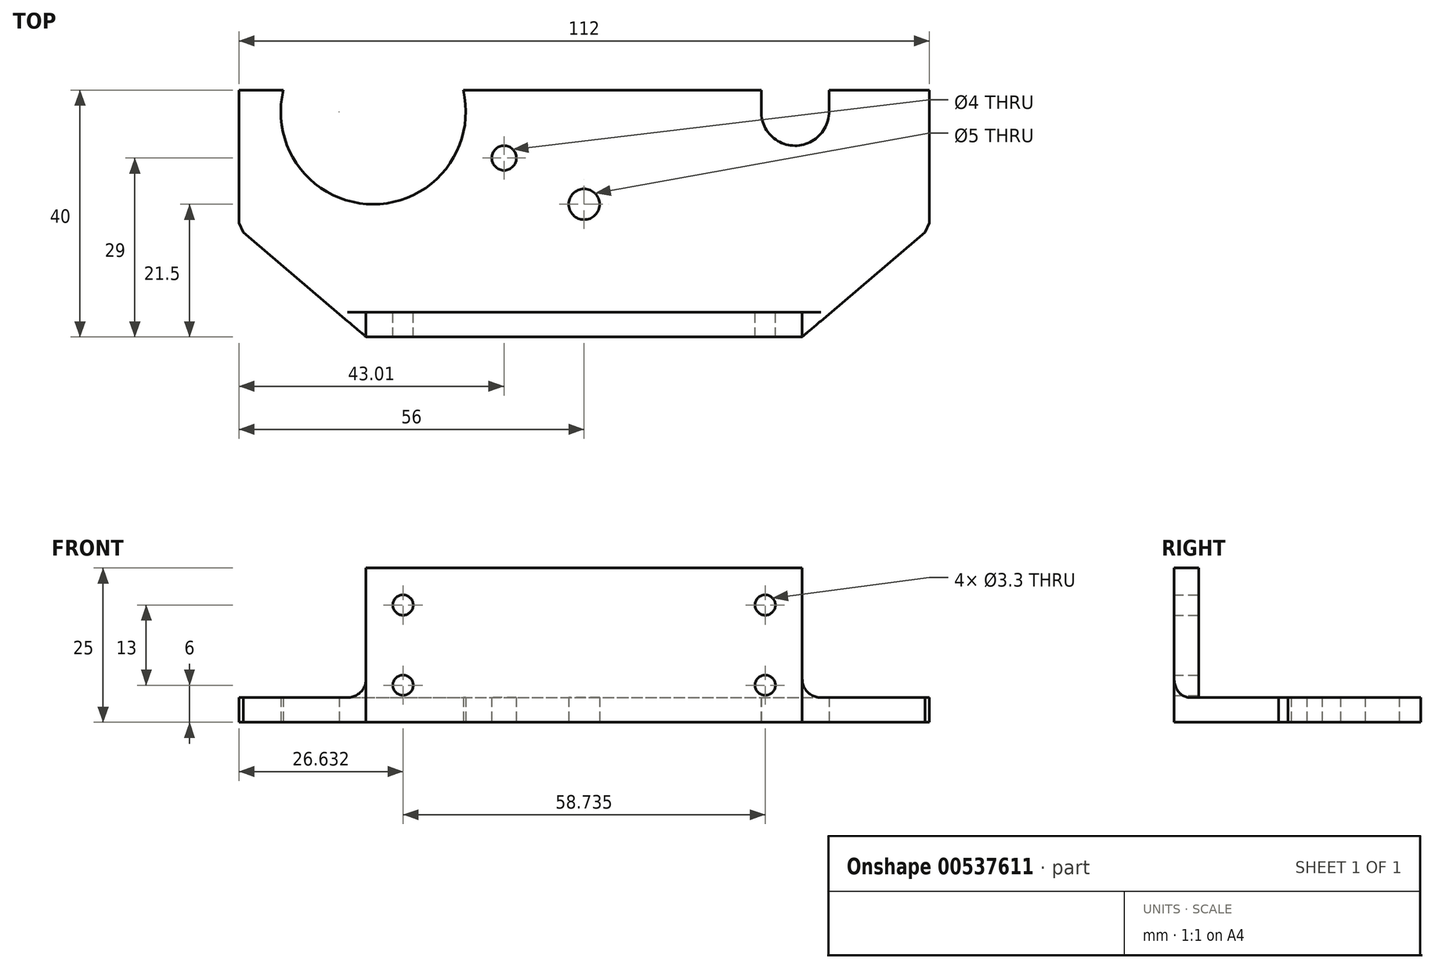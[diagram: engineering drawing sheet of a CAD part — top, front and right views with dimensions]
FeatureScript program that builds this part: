
annotation { "Feature Type Name" : "Feature", "Feature Type Description" : "" }
export const myFeature = defineFeature(function(context is Context, id is Id, definition is map)
    precondition{}
    {
        {
            var Q0;
            Q0=qCreatedBy(makeId("Top.planeOp"),FACE);
            var sketch = newSketch(context, id + "F0", { "sketchPlane" : qUnion([Q0])});
            skCircle(sketch, "E0", {"center": v(0, 0) * mm, "radius": 2.5 * mm});
            skCircle(sketch, "E1", {"center": v(0, 0) * mm, "radius": 18.5 * mm});
            skCircle(sketch, "E2", {"center": v(0, 0) * mm, "radius": 7.5 * mm});
            skCircle(sketch, "E3", {"center": v(-13, 7.5) * mm, "radius": 7.5 * mm});
            skCircle(sketch, "E4", {"center": v(-34.2, 15) * mm, "radius": 15 * mm});
            skCircle(sketch, "E5", {"center": v(-13, 7.5) * mm, "radius": 2 * mm});
            skCircle(sketch, "E6", {"center": v(-34.2, 15) * mm, "radius": 5.5 * mm});
            skLineSegment(sketch, "E7", {"start": v(0, 18.5) * mm, "end": v(-55, 18.5) * mm});
            skLineSegment(sketch, "E8", {"start": v(-55, 18.5) * mm, "end": v(-55, -3.5) * mm});
            skLineSegment(sketch, "E9", {"start": v(0, 18.5) * mm, "end": v(55, 18.5) * mm});
            skLineSegment(sketch, "E10", {"start": v(55, 18.5) * mm, "end": v(55, -3.5) * mm});
            skLineSegment(sketch, "E11", {"start": v(0, -20.5) * mm, "end": v(35, -20.5) * mm});
            skLineSegment(sketch, "E12", {"start": v(35, -20.5) * mm, "end": v(55, -3.5) * mm});
            skLineSegment(sketch, "E13", {"start": v(0, -20.5) * mm, "end": v(-35, -20.5) * mm});
            skLineSegment(sketch, "E14", {"start": v(-35, -20.5) * mm, "end": v(-55, -3.5) * mm});
            skLineSegment(sketch, "E15", {"start": v(-39.7, 14.97) * mm, "end": v(-39.7, 18.5) * mm});
            skLineSegment(sketch, "E16", {"start": v(-28.7, 15.1) * mm, "end": v(-28.76, 18.5) * mm});
            skCircle(sketch, "E17.MirrorC", {"center": v(34.2, 15) * mm, "radius": 5.5 * mm});
            skLineSegment(sketch, "E18.MirrorCS", {"start": v(28.7, 15.1) * mm, "end": v(28.76, 18.5) * mm});
            skLineSegment(sketch, "E19.MirrorCS", {"start": v(39.7, 14.97) * mm, "end": v(39.7, 18.5) * mm});
            skLineSegment(sketch, "E20.0", {"start": v(-56, 18.5) * mm, "end": v(-56, -3.96) * mm});
            skLineSegment(sketch, "E20.1", {"start": v(-35.37, -21.5) * mm, "end": v(-56, -3.96) * mm});
            skLineSegment(sketch, "E20.2", {"start": v(56, 18.5) * mm, "end": v(56, -3.96) * mm});
            skLineSegment(sketch, "E20.3", {"start": v(35.37, -21.5) * mm, "end": v(56, -3.96) * mm});
            skLineSegment(sketch, "E20.4", {"start": v(0, -21.5) * mm, "end": v(35.37, -21.5) * mm});
            skLineSegment(sketch, "E20.5", {"start": v(0, -21.5) * mm, "end": v(-35.37, -21.5) * mm});
            skLineSegment(sketch, "E21", {"start": v(56, 18.5) * mm, "end": v(55, 18.5) * mm});
            skLineSegment(sketch, "E22", {"start": v(-55, 18.5) * mm, "end": v(-56, 18.5) * mm});
            skSolve(sketch);
        }
        {
            var Q0;
            {var subQ12=sQuery(id+"F0.wireOp",EDGE,"E8");Q0=makeQuery(id+"F0.imprint","IMPRINT",FACE,{"disambiguationData":[TD([[makeQuery(id+"F0.imprint","IMPRINT",EDGE,{"derivedFrom":subQ12}),1.0]])]});}
            var Q1;
            {var subQ1=sQuery(id+"F0.wireOp",EDGE,"E2");Q1=makeQuery(id+"F0.imprint","IMPRINT",FACE,{"disambiguationData":[TD([[makeQuery(id+"F0.imprint","IMPRINT",EDGE,{"derivedFrom":subQ1}),-1.0]])]});}
            var Q2;
            Q2=makeQuery(id+"F0.imprint","IMPRINT",FACE,{"disambiguationData":[TD([[makeQuery(id+"F0.imprint","IMPRINT",EDGE,{"derivedFrom":sQuery(id+"F0.wireOp",EDGE,"E0")}),-1.0]])]});
            var Q3;
            Q3=makeQuery(id+"F0.imprint","IMPRINT",FACE,{"disambiguationData":[TD([[makeQuery(id+"F0.imprint","IMPRINT",EDGE,{"derivedFrom":sQuery(id+"F0.wireOp",EDGE,"E5")}),-1.0]])]});
            var Q4;
            {var subQ0=sQuery(id+"F0.wireOp",EDGE,"E3");var subQ1=sQuery(id+"F0.wireOp",EDGE,"E1");var subQ2=makeQuery(id+"F0.imprint","INTERSECT",VERTEX,{"disambiguationData":[OD(0.0)],"derivedFrom":[subQ1,subQ0]});Q4=makeQuery(id+"F0.imprint","IMPRINT",FACE,{"disambiguationData":[TD([[makeQuery(id+"F0.imprint","IMPRINT",EDGE,{"disambiguationData":[TD([[subQ2,-1.0]])],"derivedFrom":subQ1}),-1.0]])]});}
            var Q5;
            {var subQ1=sQuery(id+"F0.wireOp",EDGE,"E1");var subQ3=sQuery(id+"F0.wireOp",EDGE,"E3");var subQ4=makeQuery(id+"F0.imprint","INTERSECT",VERTEX,{"disambiguationData":[OD(0.0)],"derivedFrom":[subQ1,subQ3]});Q5=makeQuery(id+"F0.imprint","IMPRINT",FACE,{"disambiguationData":[TD([[makeQuery(id+"F0.imprint","IMPRINT",EDGE,{"disambiguationData":[TD([[subQ4,-1.0]])],"derivedFrom":subQ3}),-1.0]])]});}
            var Q6;
            {var subQ3=sQuery(id+"F0.wireOp",EDGE,"E15");Q6=makeQuery(id+"F0.imprint","IMPRINT",FACE,{"disambiguationData":[TD([[makeQuery(id+"F0.imprint","IMPRINT",EDGE,{"derivedFrom":subQ3}),1.0]])]});}
            var Q7;
            Q7=makeQuery(id+"F0.imprint","IMPRINT",FACE,{"disambiguationData":[TD([[makeQuery(id+"F0.imprint","IMPRINT",EDGE,{"derivedFrom":sQuery(id+"F0.wireOp",EDGE,"E8")}),-1.0]])]});
            extrude(context, id + "F1", {"entities" : qUnion([Q0, Q1, Q2, Q3, Q4, Q5, Q6, Q7]), "depth" : 4 * mm, "offsetDistance" : 25 * mm});
        }
        {
            var Q0;
            Q0=makeQuery(id+"F1.opExtrude","CAP_FACE",FACE,{"disambiguationData":[OSD([sQuery(id+"F0.wireOp",EDGE,"E0"),sQuery(id+"F0.wireOp",EDGE,"E5"),sQuery(id+"F0.wireOp",EDGE,"E6"),sQuery(id+"F0.wireOp",EDGE,"E7"),sQuery(id+"F0.wireOp",EDGE,"E9"),sQuery(id+"F0.wireOp",EDGE,"E15"),sQuery(id+"F0.wireOp",EDGE,"E16"),sQuery(id+"F0.wireOp",EDGE,"E17.MirrorC"),sQuery(id+"F0.wireOp",EDGE,"E18.MirrorCS"),sQuery(id+"F0.wireOp",EDGE,"E19.MirrorCS"),sQuery(id+"F0.wireOp",EDGE,"E20.0"),sQuery(id+"F0.wireOp",EDGE,"E20.1"),sQuery(id+"F0.wireOp",EDGE,"E20.2"),sQuery(id+"F0.wireOp",EDGE,"E20.3"),sQuery(id+"F0.wireOp",EDGE,"E20.4"),sQuery(id+"F0.wireOp",EDGE,"E20.5"),sQuery(id+"F0.wireOp",EDGE,"E21"),sQuery(id+"F0.wireOp",EDGE,"E22")])],"isStart":false});
            var sketch = newSketch(context, id + "F2", { "sketchPlane" : qUnion([Q0])});
            skLineSegment(sketch, "E23", {"start": v(-40.07, -17.5) * mm, "end": v(40.07, -17.5) * mm});
            skSolve(sketch);
        }
        {
            var Q0;
            {var subQ0=sQuery(id+"F2.wireOp",EDGE,"E23");Q0=makeQuery(id+"F2.imprint","IMPRINT",FACE,{"disambiguationData":[TD([[makeQuery(id+"F2.imprint","IMPRINT",EDGE,{"derivedFrom":subQ0}),-1.0]])]});}
            extrude(context, id + "F3", {"entities" : qUnion([Q0]), "operationType" : NewBodyOperationType.ADD, "depth" : 21 * mm, "offsetDistance" : 25 * mm});
        }
        {
            var Q0;
            {var subQ0=sQuery(id+"F0.wireOp",EDGE,"E20.5");var subQ1=sQuery(id+"F0.wireOp",EDGE,"E20.4");Q0=makeQuery(id+"F3.boolean.opBoolean","MERGE",FACE,{"derivedFrom":[makeQuery(id+"F1.opExtrude","SWEPT_FACE",FACE,{"disambiguationData":[OSD([subQ1,subQ0])]}),makeQuery(id+"F3.opExtrude","SWEPT_FACE",FACE,{"disambiguationData":[OSD([subQ1,subQ0])]})]});}
            var sketch = newSketch(context, id + "F4", { "sketchPlane" : qUnion([Q0])});
            skPoint(sketch, "E24", {"position": v(-29.37, 19) * mm});
            skPoint(sketch, "E25", {"position": v(-29.37, 6) * mm});
            skLineSegment(sketch, "E26.bottom", {"start": v(-40.07, 25) * mm, "end": v(-35.37, 25) * mm});
            skLineSegment(sketch, "E26.top", {"start": v(-40.07, 4) * mm, "end": v(-38.37, 4) * mm});
            skLineSegment(sketch, "E26.left", {"start": v(-40.07, 25) * mm, "end": v(-40.07, 4) * mm});
            skLineSegment(sketch, "E26.right", {"start": v(-35.37, 25) * mm, "end": v(-35.37, 7) * mm});
            skPoint(sketch, "E27.visualSharp", {"position": v(-35.37, 4) * mm});
            skArc(sketch, "E27.filletArc", {"start": v(-38.37, 4) * mm, "mid": v(-36.25, 4.88) * mm, "end": v(-35.37, 7) * mm});
            skLineSegment(sketch, "E28.MirrorCS", {"start": v(35.37, 25) * mm, "end": v(35.37, 7) * mm});
            skArc(sketch, "E29.MirrorCS", {"start": v(38.37, 4) * mm, "mid": v(36.25, 4.88) * mm, "end": v(35.37, 7) * mm});
            skLineSegment(sketch, "E30.MirrorCS", {"start": v(40.07, 4) * mm, "end": v(38.37, 4) * mm});
            skLineSegment(sketch, "E31.MirrorCS", {"start": v(40.07, 25) * mm, "end": v(40.07, 4) * mm});
            skLineSegment(sketch, "E32.MirrorCS", {"start": v(40.07, 25) * mm, "end": v(35.37, 25) * mm});
            skPoint(sketch, "E33.MirrorP", {"position": v(29.37, 19) * mm});
            skPoint(sketch, "E34.MirrorP", {"position": v(29.37, 6) * mm});
            skSolve(sketch);
        }
        {
            var Q0;
            Q0 = qSketchRegion(id + "F4", true);
            extrude(context, id + "F5", {"entities" : qUnion([Q0]), "operationType" : NewBodyOperationType.REMOVE, "oppositeDirection" : true, "depth" : 25 * mm, "offsetDistance" : 25 * mm});
        }
        {
            var Q0;
            Q0=sQuery(id+"F4.wireOp",VERTEX,"E24");
            var Q1;
            Q1=sQuery(id+"F4.wireOp",VERTEX,"E25");
            var Q2;
            Q2=sQuery(id+"F4.wireOp",VERTEX,"E34.MirrorP");
            var Q3;
            Q3=sQuery(id+"F4.wireOp",VERTEX,"E33.MirrorP");
            var Q4;
            Q4=makeQuery(id+"F1.opExtrude","SWEPT_BODY",BODY,{"disambiguationData":[OSD([sQuery(id+"F0.wireOp",EDGE,"E0"),sQuery(id+"F0.wireOp",EDGE,"E5"),sQuery(id+"F0.wireOp",EDGE,"E6"),sQuery(id+"F0.wireOp",EDGE,"E7"),sQuery(id+"F0.wireOp",EDGE,"E9"),sQuery(id+"F0.wireOp",EDGE,"E15"),sQuery(id+"F0.wireOp",EDGE,"E16"),sQuery(id+"F0.wireOp",EDGE,"E17.MirrorC"),sQuery(id+"F0.wireOp",EDGE,"E18.MirrorCS"),sQuery(id+"F0.wireOp",EDGE,"E19.MirrorCS"),sQuery(id+"F0.wireOp",EDGE,"E20.0"),sQuery(id+"F0.wireOp",EDGE,"E20.1"),sQuery(id+"F0.wireOp",EDGE,"E20.2"),sQuery(id+"F0.wireOp",EDGE,"E20.3"),sQuery(id+"F0.wireOp",EDGE,"E20.4"),sQuery(id+"F0.wireOp",EDGE,"E20.5"),sQuery(id+"F0.wireOp",EDGE,"E21"),sQuery(id+"F0.wireOp",EDGE,"E22")])]});
            hole(context, id + "F6", {"style" : HoleStyle.SIMPLE, "endStyle" : HoleEndStyle.THROUGH, "standardTappedOrClearance" : lookupTablePath({ "standard" : "ISO", "engagement" : "75%", "pitch" : "0.7 mm", "size" : "M4", "type" : "Tapped" }), "standardBlindInLast" : lookupTablePath({ "standard" : "ISO", "engagement" : "75%", "pitch" : "0.7 mm", "size" : "M4", "type" : "Tapped" }), "holeDiameter" : 3.3 * mm, "showTappedDepth" : true, "isTappedThrough" : true, "tappedDepth" : 12 * mm, "tapClearance" : 3, "locations" : qUnion([Q0, Q1, Q2, Q3]), "scope" : qUnion([Q4]), "majorDiameter" : 4 * mm});
        }
        {
            var Q0;
            Q0=makeQuery(id+"F1.opExtrude","SWEPT_EDGE",EDGE,{"disambiguationData":[OSD([sQuery(id+"F0.wireOp",EDGE,"E20.0"),sQuery(id+"F0.wireOp",EDGE,"E20.1")])]});
            var Q1;
            Q1=makeQuery(id+"F1.opExtrude","SWEPT_EDGE",EDGE,{"disambiguationData":[OSD([sQuery(id+"F0.wireOp",EDGE,"E20.2"),sQuery(id+"F0.wireOp",EDGE,"E20.3")])]});
            chamfer(context, id + "F7", {"entities" : qUnion([Q0, Q1]), "width" : 2 * mm, "tangentPropagation" : true});
        }
    });
